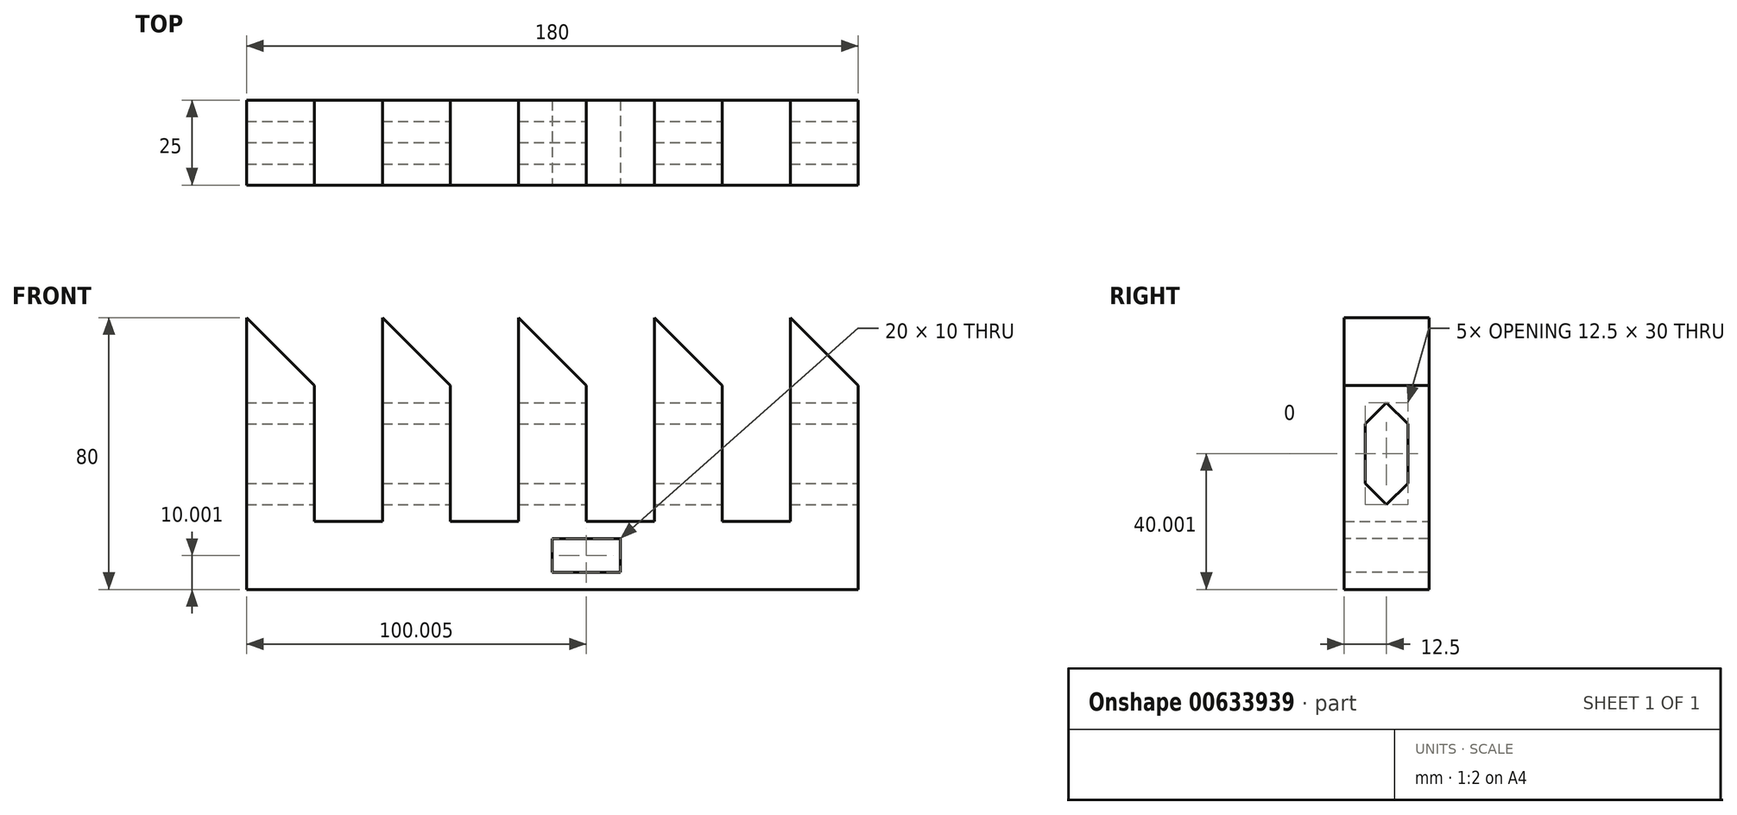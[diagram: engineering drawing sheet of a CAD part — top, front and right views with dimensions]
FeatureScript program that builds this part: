
annotation { "Feature Type Name" : "Feature", "Feature Type Description" : "" }
export const myFeature = defineFeature(function(context is Context, id is Id, definition is map)
    precondition{}
    {
        {
            var Q0;
            Q0=qCreatedBy(makeId("Front.planeOp"),FACE);
            var sketch = newSketch(context, id + "F0", { "sketchPlane" : qUnion([Q0])});
            skLineSegment(sketch, "E0.top", {"start": v(-46.6, 1.92) * mm, "end": v(133.4, 1.92) * mm});
            skLineSegment(sketch, "E0.left", {"start": v(-46.6, 21.92) * mm, "end": v(-46.6, 1.92) * mm});
            skLineSegment(sketch, "E0.right", {"start": v(133.4, 21.92) * mm, "end": v(133.4, 1.92) * mm});
            skLineSegment(sketch, "E1.bottom", {"start": v(-46.6, 21.92) * mm, "end": v(-26.6, 21.92) * mm});
            skLineSegment(sketch, "E1.top", {"start": v(-46.6, 81.92) * mm, "end": v(-26.6, 81.92) * mm});
            skLineSegment(sketch, "E1.left", {"start": v(-46.6, 21.92) * mm, "end": v(-46.6, 81.92) * mm});
            skLineSegment(sketch, "E1.right", {"start": v(-26.6, 21.92) * mm, "end": v(-26.6, 81.92) * mm});
            skLineSegment(sketch, "E2.bottom", {"start": v(-6.6, 21.92) * mm, "end": v(13.4, 21.92) * mm});
            skLineSegment(sketch, "E2.top", {"start": v(-6.6, 81.92) * mm, "end": v(13.4, 81.92) * mm});
            skLineSegment(sketch, "E2.left", {"start": v(-6.6, 21.92) * mm, "end": v(-6.6, 81.92) * mm});
            skLineSegment(sketch, "E2.right", {"start": v(13.4, 21.92) * mm, "end": v(13.4, 81.92) * mm});
            skLineSegment(sketch, "E3.bottom", {"start": v(33.4, 21.92) * mm, "end": v(53.4, 21.92) * mm});
            skLineSegment(sketch, "E3.top", {"start": v(33.4, 81.92) * mm, "end": v(53.4, 81.92) * mm});
            skLineSegment(sketch, "E3.left", {"start": v(33.4, 21.92) * mm, "end": v(33.4, 81.92) * mm});
            skLineSegment(sketch, "E3.right", {"start": v(53.4, 21.92) * mm, "end": v(53.4, 81.92) * mm});
            skLineSegment(sketch, "E4.bottom", {"start": v(73.4, 21.92) * mm, "end": v(93.4, 21.92) * mm});
            skLineSegment(sketch, "E4.top", {"start": v(73.4, 81.92) * mm, "end": v(93.4, 81.92) * mm});
            skLineSegment(sketch, "E4.left", {"start": v(73.4, 21.92) * mm, "end": v(73.4, 81.92) * mm});
            skLineSegment(sketch, "E4.right", {"start": v(93.4, 21.92) * mm, "end": v(93.4, 81.92) * mm});
            skLineSegment(sketch, "E5.bottom", {"start": v(133.4, 21.92) * mm, "end": v(113.4, 21.92) * mm});
            skLineSegment(sketch, "E5.top", {"start": v(133.4, 81.92) * mm, "end": v(113.4, 81.92) * mm});
            skLineSegment(sketch, "E5.left", {"start": v(133.4, 21.92) * mm, "end": v(133.4, 81.92) * mm});
            skLineSegment(sketch, "E5.right", {"start": v(113.4, 21.92) * mm, "end": v(113.4, 81.92) * mm});
            skLineSegment(sketch, "E6", {"start": v(113.4, 21.92) * mm, "end": v(93.4, 21.92) * mm});
            skLineSegment(sketch, "E7", {"start": v(73.4, 21.92) * mm, "end": v(53.4, 21.92) * mm});
            skLineSegment(sketch, "E8", {"start": v(33.4, 21.92) * mm, "end": v(13.4, 21.92) * mm});
            skLineSegment(sketch, "E9", {"start": v(-6.6, 21.92) * mm, "end": v(-26.6, 21.92) * mm});
            skSolve(sketch);
        }
        {
            var Q0;
            Q0 = qSketchRegion(id + "F0", true);
            extrude(context, id + "F1", {"entities" : qUnion([Q0]), "depth" : 25 * mm, "offsetDistance" : 25 * mm});
        }
        {
            var Q0;
            Q0=makeQuery(id+"F1.opExtrude","SWEPT_FACE",FACE,{"disambiguationData":[OSD([sQuery(id+"F0.wireOp",EDGE,"E0.right"),sQuery(id+"F0.wireOp",EDGE,"E5.left")])]});
            var sketch = newSketch(context, id + "F2", { "sketchPlane" : qUnion([Q0])});
            skLineSegment(sketch, "E10", {"start": v(-25, 41.92) * mm, "end": v(0, 41.92) * mm, "construction": true});
            skLineSegment(sketch, "E11.bottom", {"start": v(-18.75, 26.92) * mm, "end": v(-6.25, 26.92) * mm, "construction": true});
            skLineSegment(sketch, "E11.top", {"start": v(-18.75, 56.92) * mm, "end": v(-6.25, 56.92) * mm, "construction": true});
            skLineSegment(sketch, "E11.left", {"start": v(-18.75, 33.17) * mm, "end": v(-18.75, 50.67) * mm});
            skLineSegment(sketch, "E11.right", {"start": v(-6.25, 33.17) * mm, "end": v(-6.25, 50.67) * mm});
            skLineSegment(sketch, "E12", {"start": v(-12.5, 41.92) * mm, "end": v(-12.5, 53.1) * mm, "construction": true});
            skLineSegment(sketch, "E13", {"start": v(-12.5, 56.92) * mm, "end": v(-18.75, 50.67) * mm});
            skLineSegment(sketch, "E14", {"start": v(-12.5, 56.92) * mm, "end": v(-6.25, 50.67) * mm});
            skLineSegment(sketch, "E15", {"start": v(-12.5, 26.92) * mm, "end": v(-18.75, 33.17) * mm});
            skLineSegment(sketch, "E16", {"start": v(-12.5, 26.92) * mm, "end": v(-6.25, 33.17) * mm});
            skSolve(sketch);
        }
        {
            var Q0;
            Q0 = qSketchRegion(id + "F2", true);
            extrude(context, id + "F3", {"entities" : qUnion([Q0]), "operationType" : NewBodyOperationType.REMOVE, "endBound" : BoundingType.THROUGH_ALL, "oppositeDirection" : true, "depth" : 25 * mm, "offsetDistance" : 25 * mm});
        }
        {
            var Q0;
            Q0=makeQuery(id+"F1.opExtrude","CAP_FACE",FACE,{"disambiguationData":[OSD([sQuery(id+"F0.wireOp",EDGE,"E0.top"),sQuery(id+"F0.wireOp",EDGE,"E0.left"),sQuery(id+"F0.wireOp",EDGE,"E0.right"),sQuery(id+"F0.wireOp",EDGE,"E1.top"),sQuery(id+"F0.wireOp",EDGE,"E1.left"),sQuery(id+"F0.wireOp",EDGE,"E1.right"),sQuery(id+"F0.wireOp",EDGE,"E2.top"),sQuery(id+"F0.wireOp",EDGE,"E2.left"),sQuery(id+"F0.wireOp",EDGE,"E2.right"),sQuery(id+"F0.wireOp",EDGE,"E3.top"),sQuery(id+"F0.wireOp",EDGE,"E3.left"),sQuery(id+"F0.wireOp",EDGE,"E3.right"),sQuery(id+"F0.wireOp",EDGE,"E4.top"),sQuery(id+"F0.wireOp",EDGE,"E4.left"),sQuery(id+"F0.wireOp",EDGE,"E4.right"),sQuery(id+"F0.wireOp",EDGE,"E5.top"),sQuery(id+"F0.wireOp",EDGE,"E5.left"),sQuery(id+"F0.wireOp",EDGE,"E5.right"),sQuery(id+"F0.wireOp",EDGE,"E6"),sQuery(id+"F0.wireOp",EDGE,"E7"),sQuery(id+"F0.wireOp",EDGE,"E8"),sQuery(id+"F0.wireOp",EDGE,"E9")])],"isStart":false});
            var sketch = newSketch(context, id + "F4", { "sketchPlane" : qUnion([Q0])});
            skLineSegment(sketch, "E17", {"start": v(-46.6, 81.92) * mm, "end": v(-26.6, 61.92) * mm});
            skLineSegment(sketch, "E18", {"start": v(-6.6, 81.92) * mm, "end": v(13.4, 61.92) * mm});
            skLineSegment(sketch, "E19", {"start": v(33.4, 81.92) * mm, "end": v(53.4, 61.92) * mm});
            skLineSegment(sketch, "E20", {"start": v(73.4, 81.92) * mm, "end": v(93.4, 61.92) * mm});
            skLineSegment(sketch, "E21", {"start": v(113.4, 81.92) * mm, "end": v(133.4, 61.92) * mm});
            skLineSegment(sketch, "E22", {"start": v(133.4, 61.92) * mm, "end": v(133.4, 81.92) * mm});
            skLineSegment(sketch, "E23", {"start": v(133.4, 81.92) * mm, "end": v(113.4, 81.92) * mm});
            skLineSegment(sketch, "E24", {"start": v(93.4, 61.92) * mm, "end": v(93.4, 81.92) * mm});
            skLineSegment(sketch, "E25", {"start": v(93.4, 81.92) * mm, "end": v(73.4, 81.92) * mm});
            skLineSegment(sketch, "E26", {"start": v(53.4, 61.92) * mm, "end": v(53.4, 81.92) * mm});
            skLineSegment(sketch, "E27", {"start": v(53.4, 81.92) * mm, "end": v(33.4, 81.92) * mm});
            skLineSegment(sketch, "E28", {"start": v(13.4, 61.92) * mm, "end": v(13.4, 81.92) * mm});
            skLineSegment(sketch, "E29", {"start": v(13.4, 81.92) * mm, "end": v(-6.6, 81.92) * mm});
            skLineSegment(sketch, "E30", {"start": v(-26.6, 61.92) * mm, "end": v(-26.6, 81.92) * mm});
            skLineSegment(sketch, "E31", {"start": v(-26.6, 81.92) * mm, "end": v(-46.6, 81.92) * mm});
            skSolve(sketch);
        }
        {
            var Q0;
            Q0 = qSketchRegion(id + "F4", true);
            extrude(context, id + "F5", {"entities" : qUnion([Q0]), "operationType" : NewBodyOperationType.REMOVE, "endBound" : BoundingType.THROUGH_ALL, "oppositeDirection" : true, "depth" : 25 * mm, "offsetDistance" : 25 * mm});
        }
        {
            var Q0;
            Q0=makeQuery(id+"F1.opExtrude","CAP_FACE",FACE,{"disambiguationData":[OSD([sQuery(id+"F0.wireOp",EDGE,"E0.top"),sQuery(id+"F0.wireOp",EDGE,"E0.left"),sQuery(id+"F0.wireOp",EDGE,"E0.right"),sQuery(id+"F0.wireOp",EDGE,"E1.top"),sQuery(id+"F0.wireOp",EDGE,"E1.left"),sQuery(id+"F0.wireOp",EDGE,"E1.right"),sQuery(id+"F0.wireOp",EDGE,"E2.top"),sQuery(id+"F0.wireOp",EDGE,"E2.left"),sQuery(id+"F0.wireOp",EDGE,"E2.right"),sQuery(id+"F0.wireOp",EDGE,"E3.top"),sQuery(id+"F0.wireOp",EDGE,"E3.left"),sQuery(id+"F0.wireOp",EDGE,"E3.right"),sQuery(id+"F0.wireOp",EDGE,"E4.top"),sQuery(id+"F0.wireOp",EDGE,"E4.left"),sQuery(id+"F0.wireOp",EDGE,"E4.right"),sQuery(id+"F0.wireOp",EDGE,"E5.top"),sQuery(id+"F0.wireOp",EDGE,"E5.left"),sQuery(id+"F0.wireOp",EDGE,"E5.right"),sQuery(id+"F0.wireOp",EDGE,"E6"),sQuery(id+"F0.wireOp",EDGE,"E7"),sQuery(id+"F0.wireOp",EDGE,"E8"),sQuery(id+"F0.wireOp",EDGE,"E9")])],"isStart":false});
            var sketch = newSketch(context, id + "F6", { "sketchPlane" : qUnion([Q0])});
            skPoint(sketch, "E32.oppositeSnap0", {"position": v(63.4, 21.92) * mm});
            skLineSegment(sketch, "E32.bottom", {"start": v(43.4, 16.92) * mm, "end": v(63.4, 16.92) * mm});
            skLineSegment(sketch, "E32.top", {"start": v(43.4, 6.92) * mm, "end": v(63.4, 6.92) * mm});
            skLineSegment(sketch, "E32.left", {"start": v(43.4, 16.92) * mm, "end": v(43.4, 6.92) * mm});
            skLineSegment(sketch, "E32.right", {"start": v(63.4, 16.92) * mm, "end": v(63.4, 6.92) * mm});
            skLineSegment(sketch, "E33", {"start": v(53.4, 16.92) * mm, "end": v(53.4, 6.92) * mm, "construction": true});
            skLineSegment(sketch, "E34", {"start": v(48.66, 11.92) * mm, "end": v(53.4, 11.92) * mm, "construction": true});
            skSolve(sketch);
        }
        {
            var Q0;
            Q0 = qSketchRegion(id + "F6", true);
            extrude(context, id + "F7", {"entities" : qUnion([Q0]), "operationType" : NewBodyOperationType.REMOVE, "endBound" : BoundingType.THROUGH_ALL, "oppositeDirection" : true, "depth" : 25 * mm, "offsetDistance" : 25 * mm});
        }
    });
